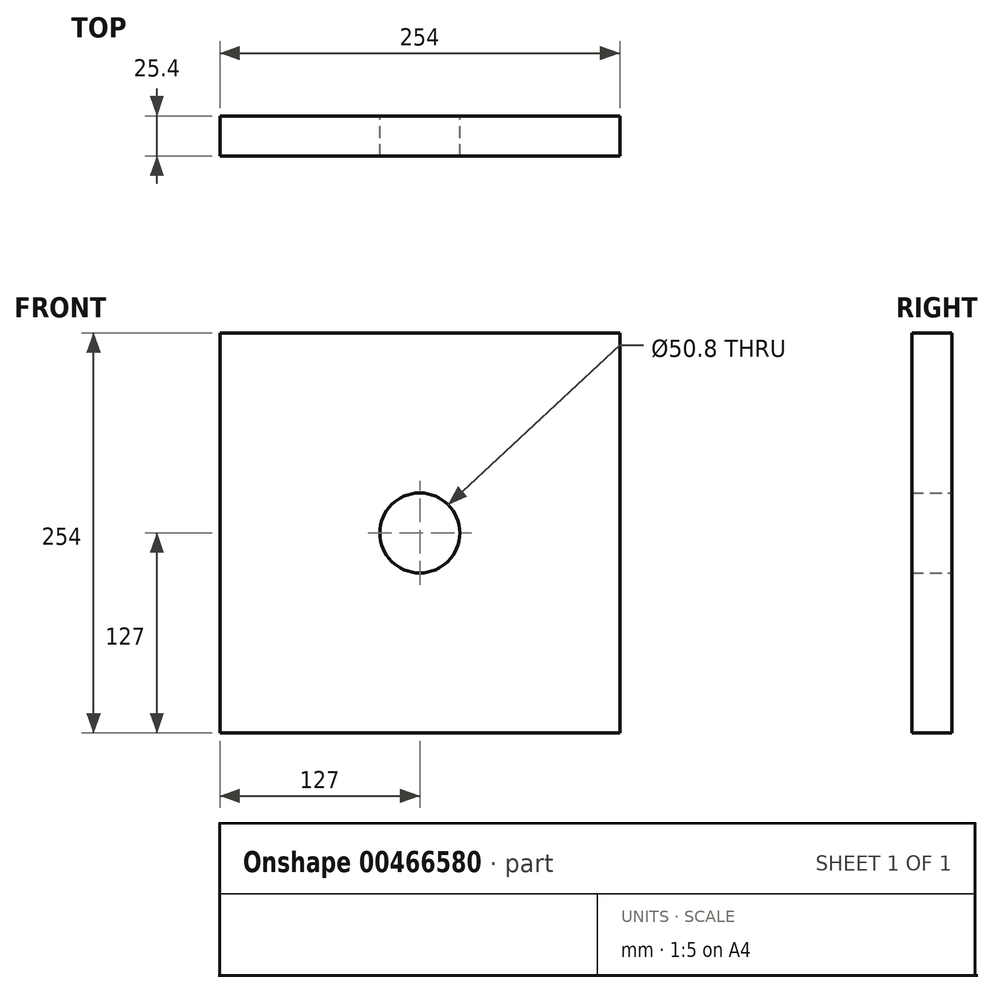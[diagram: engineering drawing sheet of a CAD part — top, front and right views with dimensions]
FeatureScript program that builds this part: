
annotation { "Feature Type Name" : "Feature", "Feature Type Description" : "" }
export const myFeature = defineFeature(function(context is Context, id is Id, definition is map)
    precondition{}
    {
        {
            var Q0;
            Q0=qCreatedBy(makeId("Front.planeOp"),FACE);
            var sketch = newSketch(context, id + "F0", { "sketchPlane" : qUnion([Q0])});
            skLineSegment(sketch, "E0.bottom", {"start": v(-127, 127) * mm, "end": v(127, 127) * mm});
            skLineSegment(sketch, "E0.top", {"start": v(-127, -127) * mm, "end": v(127, -127) * mm});
            skLineSegment(sketch, "E0.left", {"start": v(-127, 127) * mm, "end": v(-127, -127) * mm});
            skLineSegment(sketch, "E0.right", {"start": v(127, 127) * mm, "end": v(127, -127) * mm});
            skCircle(sketch, "E1", {"center": v(0, 0) * mm, "radius": 25.4 * mm});
            skSolve(sketch);
        }
        {
            var Q0;
            Q0=makeQuery(id+"F0.imprint","IMPRINT",FACE,{"disambiguationData":[TD([[makeQuery(id+"F0.imprint","IMPRINT",EDGE,{"derivedFrom":sQuery(id+"F0.wireOp",EDGE,"E0.bottom")}),-1.0]])]});
            extrude(context, id + "F1", {"entities" : qUnion([Q0]), "depth" : 25.4 * mm});
        }
    });
